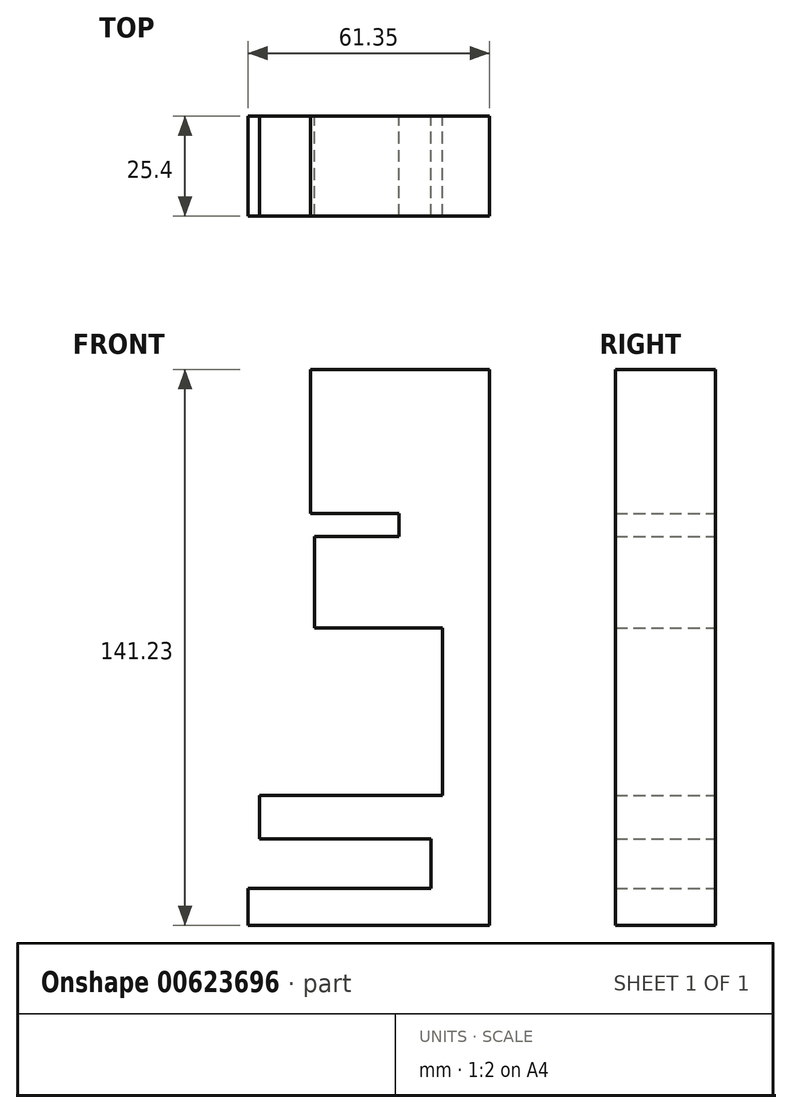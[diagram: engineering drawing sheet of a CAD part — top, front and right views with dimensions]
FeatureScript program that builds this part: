
annotation { "Feature Type Name" : "Feature", "Feature Type Description" : "" }
export const myFeature = defineFeature(function(context is Context, id is Id, definition is map)
    precondition{}
    {
        {
            var Q0;
            Q0=qCreatedBy(makeId("Front.planeOp"),FACE);
            var sketch = newSketch(context, id + "F0", { "sketchPlane" : qUnion([Q0])});
            skLineSegment(sketch, "E0.bottom", {"start": v(-45.5, 65.65) * mm, "end": v(0, 65.65) * mm});
            skLineSegment(sketch, "E0.top", {"start": v(-45.5, 29.13) * mm, "end": v(0, 29.13) * mm});
            skLineSegment(sketch, "E0.left", {"start": v(-45.5, 65.65) * mm, "end": v(-45.5, 29.13) * mm});
            skLineSegment(sketch, "E0.right", {"start": v(0, 65.65) * mm, "end": v(0, 29.13) * mm});
            skLineSegment(sketch, "E1.bottom", {"start": v(0, 29.13) * mm, "end": v(-22.96, 29.13) * mm});
            skLineSegment(sketch, "E1.top", {"start": v(0, 23.22) * mm, "end": v(-22.96, 23.22) * mm});
            skLineSegment(sketch, "E1.left", {"start": v(0, 29.13) * mm, "end": v(0, 23.22) * mm});
            skLineSegment(sketch, "E1.right", {"start": v(-22.96, 29.13) * mm, "end": v(-22.96, 23.22) * mm});
            skLineSegment(sketch, "E2.bottom", {"start": v(0, 23.22) * mm, "end": v(-44.44, 23.22) * mm});
            skLineSegment(sketch, "E2.top", {"start": v(0, 0) * mm, "end": v(-44.44, 0) * mm});
            skLineSegment(sketch, "E2.left", {"start": v(0, 23.22) * mm, "end": v(0, 0) * mm});
            skLineSegment(sketch, "E2.right", {"start": v(-44.44, 23.22) * mm, "end": v(-44.44, 0) * mm});
            skLineSegment(sketch, "E3.bottom", {"start": v(0, 0) * mm, "end": v(-11.95, 0) * mm});
            skLineSegment(sketch, "E3.top", {"start": v(0, -42.56) * mm, "end": v(-11.95, -42.56) * mm});
            skLineSegment(sketch, "E3.left", {"start": v(0, 0) * mm, "end": v(0, -42.56) * mm});
            skLineSegment(sketch, "E3.right", {"start": v(-11.95, 0) * mm, "end": v(-11.95, -42.56) * mm});
            skLineSegment(sketch, "E4.bottom", {"start": v(0, -42.56) * mm, "end": v(-58.4, -42.56) * mm});
            skLineSegment(sketch, "E4.top", {"start": v(0, -53.56) * mm, "end": v(-58.4, -53.56) * mm});
            skLineSegment(sketch, "E4.left", {"start": v(0, -42.56) * mm, "end": v(0, -53.56) * mm});
            skLineSegment(sketch, "E4.right", {"start": v(-58.4, -42.56) * mm, "end": v(-58.4, -53.56) * mm});
            skLineSegment(sketch, "E5.bottom", {"start": v(0, -53.56) * mm, "end": v(-14.9, -53.56) * mm});
            skLineSegment(sketch, "E5.top", {"start": v(0, -66.18) * mm, "end": v(-14.9, -66.18) * mm});
            skLineSegment(sketch, "E5.left", {"start": v(0, -53.56) * mm, "end": v(0, -66.18) * mm});
            skLineSegment(sketch, "E5.right", {"start": v(-14.9, -53.56) * mm, "end": v(-14.9, -66.18) * mm});
            skLineSegment(sketch, "E6.bottom", {"start": v(0, -66.18) * mm, "end": v(-61.35, -66.18) * mm});
            skLineSegment(sketch, "E6.top", {"start": v(0, -75.58) * mm, "end": v(-61.35, -75.58) * mm});
            skLineSegment(sketch, "E6.left", {"start": v(0, -66.18) * mm, "end": v(0, -75.58) * mm});
            skLineSegment(sketch, "E6.right", {"start": v(-61.35, -66.18) * mm, "end": v(-61.35, -75.58) * mm});
            skSolve(sketch);
        }
        {
            var Q0;
            Q0 = qSketchRegion(id + "F0", true);
            extrude(context, id + "F1", {"entities" : qUnion([Q0]), "depth" : 25.4 * mm, "offsetDistance" : 25.4 * mm});
        }
    });
